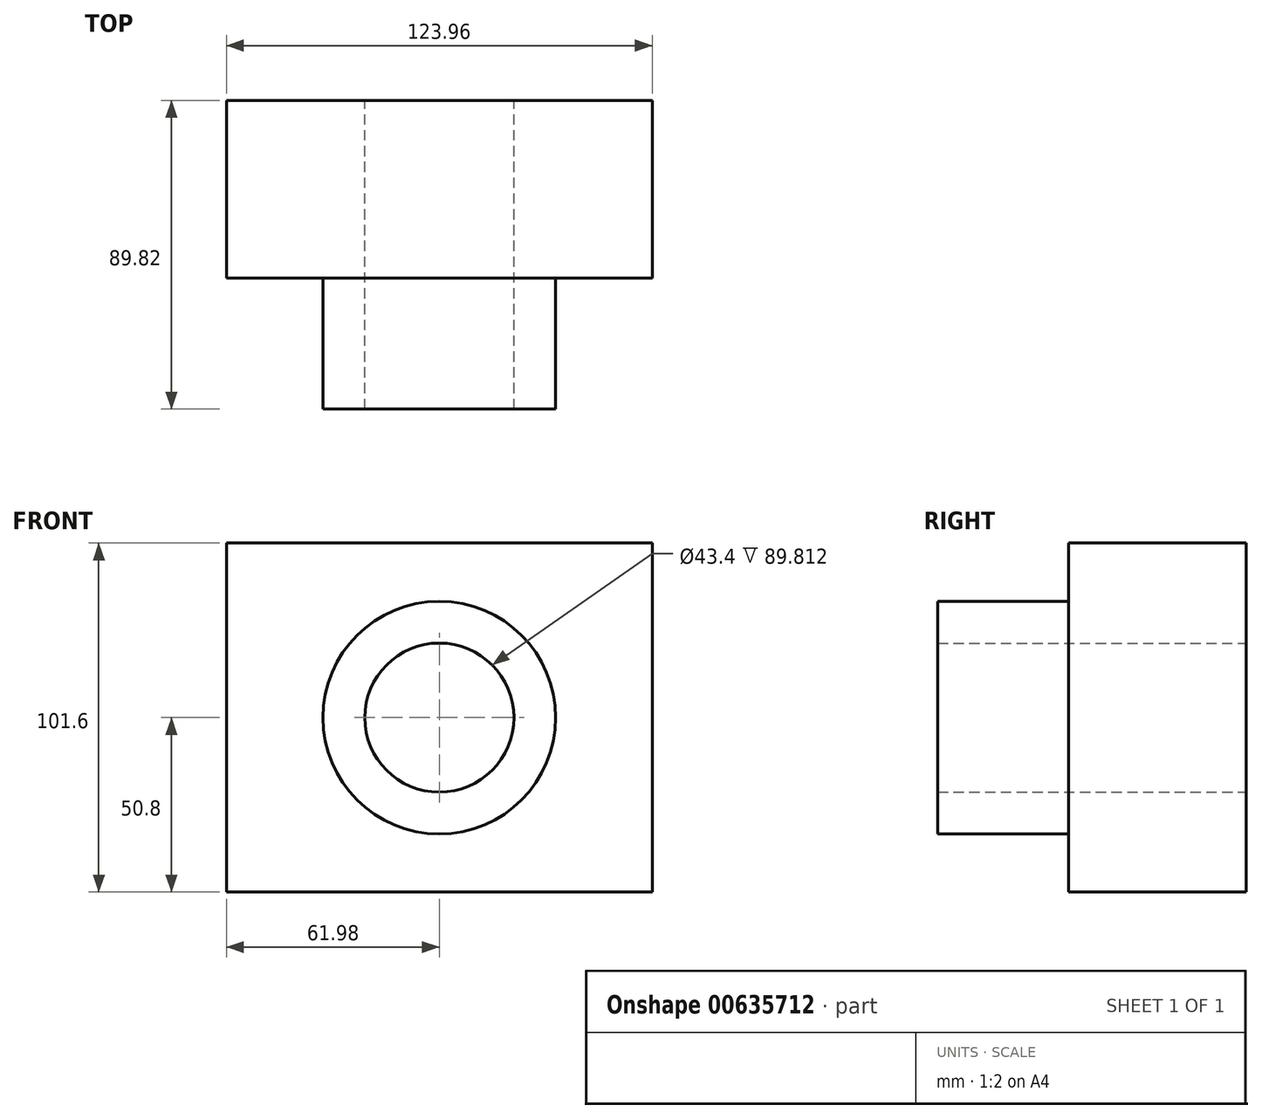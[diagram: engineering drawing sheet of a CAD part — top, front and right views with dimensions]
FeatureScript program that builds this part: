
annotation { "Feature Type Name" : "Feature", "Feature Type Description" : "" }
export const myFeature = defineFeature(function(context is Context, id is Id, definition is map)
    precondition{}
    {
        {
            var Q0;
            Q0=qCreatedBy(makeId("Top.planeOp"),FACE);
            var sketch = newSketch(context, id + "F0", { "sketchPlane" : qUnion([Q0])});
            skLineSegment(sketch, "E0.bottom", {"start": v(61.98, -25.86) * mm, "end": v(-61.98, -25.86) * mm});
            skLineSegment(sketch, "E0.top", {"start": v(61.98, 25.86) * mm, "end": v(-61.98, 25.86) * mm});
            skLineSegment(sketch, "E0.left", {"start": v(61.98, -25.86) * mm, "end": v(61.98, 25.86) * mm});
            skLineSegment(sketch, "E0.right", {"start": v(-61.98, -25.86) * mm, "end": v(-61.98, 25.86) * mm});
            skPoint(sketch, "E0.middle", {"position": v(0, 0) * mm});
            skSolve(sketch);
        }
        {
            var Q0;
            Q0=makeQuery(id+"F0.imprint","IMPRINT",FACE,{"disambiguationData":[TD([[makeQuery(id+"F0.imprint","IMPRINT",EDGE,{"derivedFrom":sQuery(id+"F0.wireOp",EDGE,"E0.bottom")}),-1.0]])]});
            extrude(context, id + "F1", {"entities" : qUnion([Q0]), "depth" : 101.6 * mm, "offsetDistance" : 25.4 * mm});
        }
        {
            var Q0;
            Q0=makeQuery(id+"F1.opExtrude","SWEPT_FACE",FACE,{"disambiguationData":[OSD([sQuery(id+"F0.wireOp",EDGE,"E0.bottom")])]});
            var sketch = newSketch(context, id + "F2", { "sketchPlane" : qUnion([Q0])});
            skCircle(sketch, "E1", {"center": v(0, 50.8) * mm, "radius": 33.88 * mm});
            skPoint(sketch, "E1.centerSnap0", {"position": v(61.98, 50.8) * mm});
            skCircle(sketch, "E2", {"center": v(0, 50.8) * mm, "radius": 21.7 * mm});
            skSolve(sketch);
        }
        {
            var Q0;
            Q0=makeQuery(id+"F2.imprint","IMPRINT",FACE,{"disambiguationData":[TD([[makeQuery(id+"F2.imprint","IMPRINT",EDGE,{"derivedFrom":sQuery(id+"F2.wireOp",EDGE,"E1")}),1.0]])]});
            extrude(context, id + "F3", {"entities" : qUnion([Q0]), "operationType" : NewBodyOperationType.ADD, "depth" : 38.1 * mm, "offsetDistance" : 25.4 * mm});
        }
        {
            var Q0;
            Q0=makeQuery(id+"F3.boolean.opBoolean","SPLIT",FACE,{"disambiguationData":[TD([makeQuery(id+"F3.opExtrude","SWEPT_FACE",FACE,{"disambiguationData":[OSD([sQuery(id+"F2.wireOp",EDGE,"E2")])]})])],"derivedFrom":makeQuery(id+"F1.opExtrude","SWEPT_FACE",FACE,{"disambiguationData":[OSD([sQuery(id+"F0.wireOp",EDGE,"E0.bottom")])]})});
            extrude(context, id + "F4", {"entities" : qUnion([Q0]), "operationType" : NewBodyOperationType.REMOVE, "oppositeDirection" : true, "depth" : 2540 * mm, "offsetDistance" : 25.4 * mm});
        }
    });
